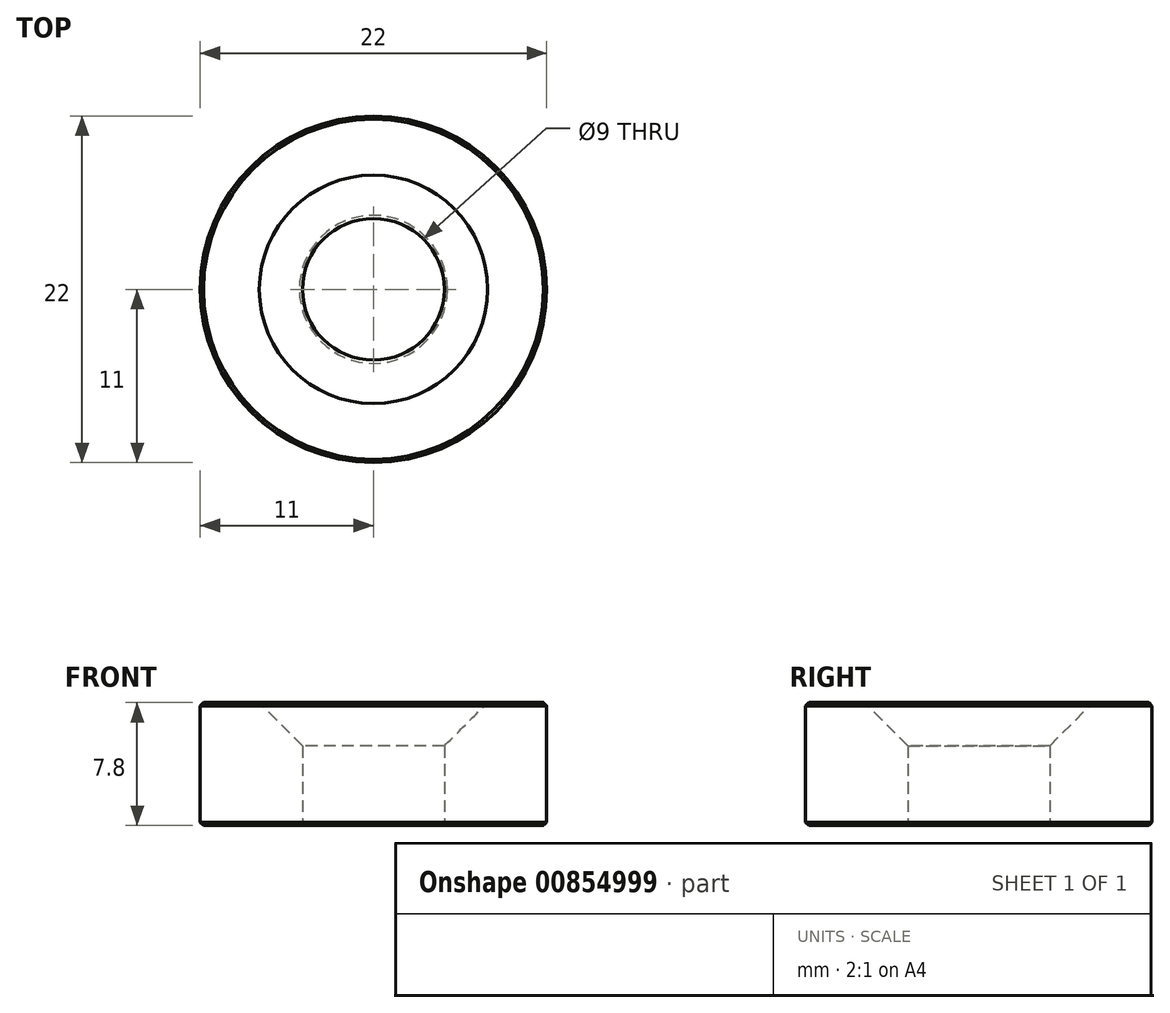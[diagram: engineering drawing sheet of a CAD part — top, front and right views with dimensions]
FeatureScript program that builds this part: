
annotation { "Feature Type Name" : "Feature", "Feature Type Description" : "" }
export const myFeature = defineFeature(function(context is Context, id is Id, definition is map)
    precondition{}
    {
        {
            var Q0;
            Q0=qCreatedBy(makeId("Top.planeOp"),FACE);
            var sketch = newSketch(context, id + "F0", { "sketchPlane" : qUnion([Q0])});
            skCircle(sketch, "E0", {"center": v(0, 0) * mm, "radius": 11 * mm});
            skCircle(sketch, "E1", {"center": v(0, 0) * mm, "radius": 4.5 * mm});
            skSolve(sketch);
        }
        {
            var Q0;
            Q0=makeQuery(id+"F0.imprint","IMPRINT",FACE,{"disambiguationData":[TD([[makeQuery(id+"F0.imprint","IMPRINT",EDGE,{"derivedFrom":sQuery(id+"F0.wireOp",EDGE,"E0")}),1.0]])]});
            extrude(context, id + "F1", {"entities" : qUnion([Q0]), "depth" : 7.8 * mm, "offsetDistance" : 25 * mm});
        }
        {
            var Q0;
            Q0=makeQuery(id+"F1.opExtrude","CAP_EDGE",EDGE,{"disambiguationData":[OSD([sQuery(id+"F0.wireOp",EDGE,"E0")])],"isStart":false});
            var Q1;
            Q1=makeQuery(id+"F1.opExtrude","CAP_EDGE",EDGE,{"disambiguationData":[OSD([sQuery(id+"F0.wireOp",EDGE,"E0")])],"isStart":true});
            var Q2;
            Q2=makeQuery(id+"F8ZHsVc7kUlFcrg_1.boolean.opBoolean","INTERSECT",EDGE,{"derivedFrom":[makeQuery(id+"F1.opExtrude","SWEPT_FACE",FACE,{"disambiguationData":[OSD([sQuery(id+"F0.wireOp",EDGE,"E1")])]}),makeQuery(id+"F8ZHsVc7kUlFcrg_1.opExtrude","CAP_FACE",FACE,{"disambiguationData":[OSD([sQuery(id+"FoxCfDz5NVmvw8K_1.wireOp",EDGE,"RIeFjllb-qMbl-JkgV-GW7n-yeymAF3cbqiI")])],"isStart":false})]});
            var Q3;
            Q3=makeQuery(id+"F1.opExtrude","CAP_EDGE",EDGE,{"disambiguationData":[OSD([sQuery(id+"F0.wireOp",EDGE,"E1")])],"isStart":true});
            chamfer(context, id + "F2", {"entities" : qUnion([Q0, Q1, Q2, Q3]), "width" : .2 * mm, "tangentPropagation" : true});
        }
        {
            var Q0;
            Q0=makeQuery(id+"F1.opExtrude","CAP_EDGE",EDGE,{"disambiguationData":[OSD([sQuery(id+"F0.wireOp",EDGE,"E1")])],"isStart":false});
            chamfer(context, id + "F3", {"entities" : qUnion([Q0]), "width" : 2.75 * mm, "tangentPropagation" : true});
        }
    });
